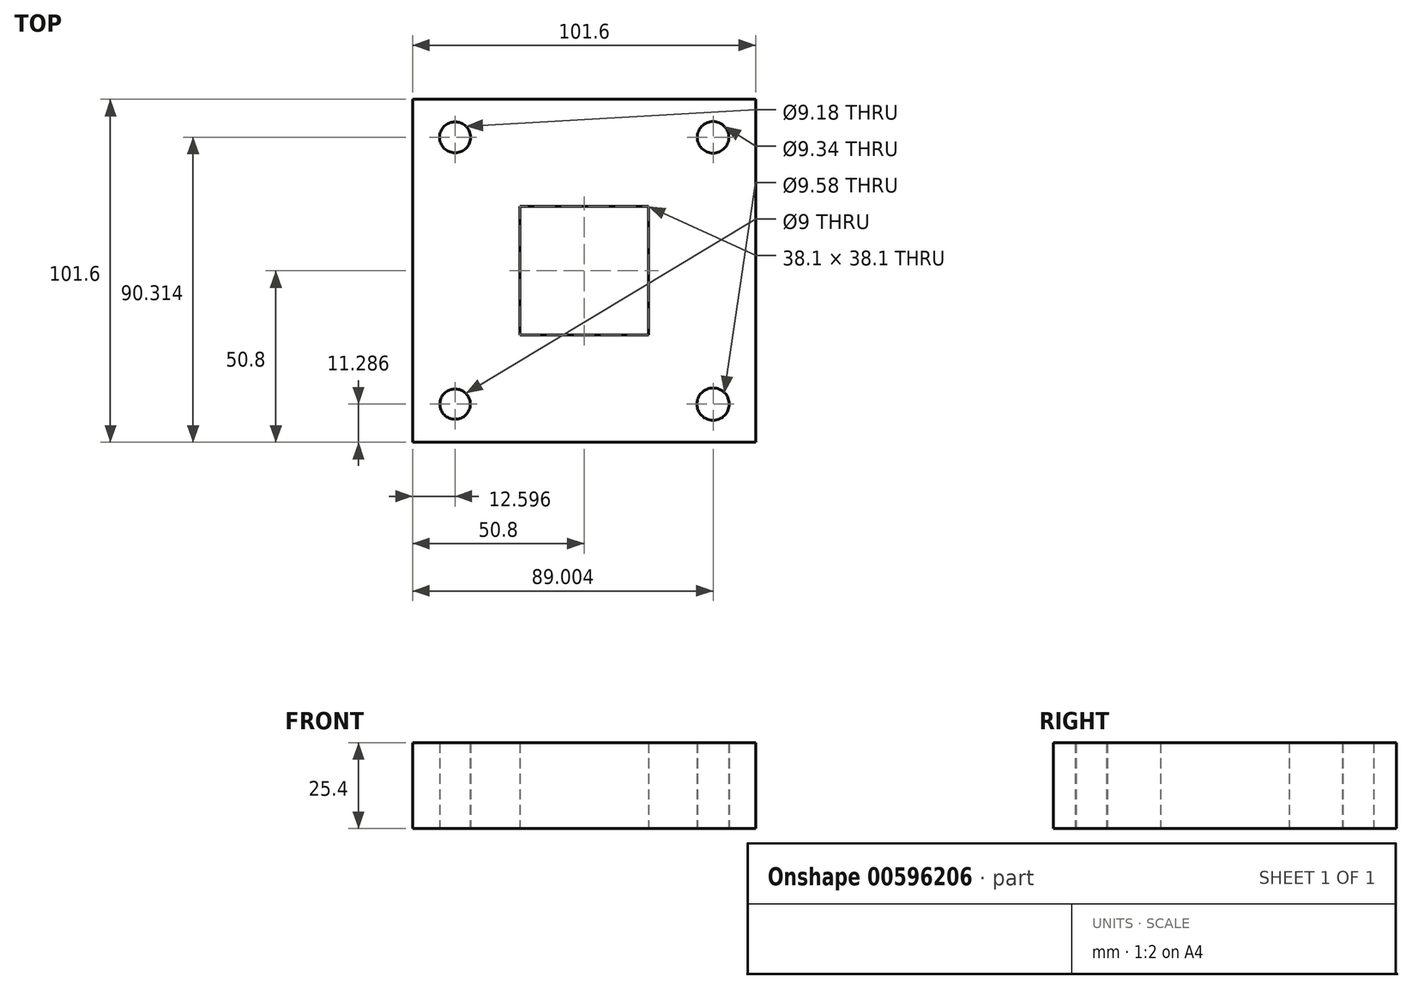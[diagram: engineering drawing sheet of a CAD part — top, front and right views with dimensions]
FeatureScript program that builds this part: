
annotation { "Feature Type Name" : "Feature", "Feature Type Description" : "" }
export const myFeature = defineFeature(function(context is Context, id is Id, definition is map)
    precondition{}
    {
        {
            var Q0;
            Q0=qCreatedBy(makeId("Top.planeOp"),FACE);
            var sketch = newSketch(context, id + "F0", { "sketchPlane" : qUnion([Q0])});
            skLineSegment(sketch, "E0.bottom", {"start": v(-50.8, 50.8) * mm, "end": v(50.8, 50.8) * mm});
            skLineSegment(sketch, "E0.top", {"start": v(-50.8, -50.8) * mm, "end": v(50.8, -50.8) * mm});
            skLineSegment(sketch, "E0.left", {"start": v(-50.8, 50.8) * mm, "end": v(-50.8, -50.8) * mm});
            skLineSegment(sketch, "E0.right", {"start": v(50.8, 50.8) * mm, "end": v(50.8, -50.8) * mm});
            skLineSegment(sketch, "E1.bottom", {"start": v(19.05, 19.05) * mm, "end": v(-19.05, 19.05) * mm});
            skLineSegment(sketch, "E1.top", {"start": v(19.05, -19.05) * mm, "end": v(-19.05, -19.05) * mm});
            skLineSegment(sketch, "E1.left", {"start": v(19.05, 19.05) * mm, "end": v(19.05, -19.05) * mm});
            skLineSegment(sketch, "E1.right", {"start": v(-19.05, 19.05) * mm, "end": v(-19.05, -19.05) * mm});
            skCircle(sketch, "E2", {"center": v(-38.2, 39.51) * mm, "radius": 4.59 * mm});
            skCircle(sketch, "E3", {"center": v(38.2, 39.51) * mm, "radius": 4.67 * mm});
            skCircle(sketch, "E4", {"center": v(38.2, -39.51) * mm, "radius": 4.79 * mm});
            skCircle(sketch, "E5", {"center": v(-38.2, -39.51) * mm, "radius": 4.5 * mm});
            skSolve(sketch);
        }
        {
            var Q0;
            Q0=makeQuery(id+"F0.imprint","IMPRINT",FACE,{"disambiguationData":[TD([[makeQuery(id+"F0.imprint","IMPRINT",EDGE,{"derivedFrom":sQuery(id+"F0.wireOp",EDGE,"E0.bottom")}),-1.0]])]});
            extrude(context, id + "F1", {"entities" : qUnion([Q0]), "depth" : 25.4 * mm, "offsetDistance" : 25.4 * mm});
        }
    });
